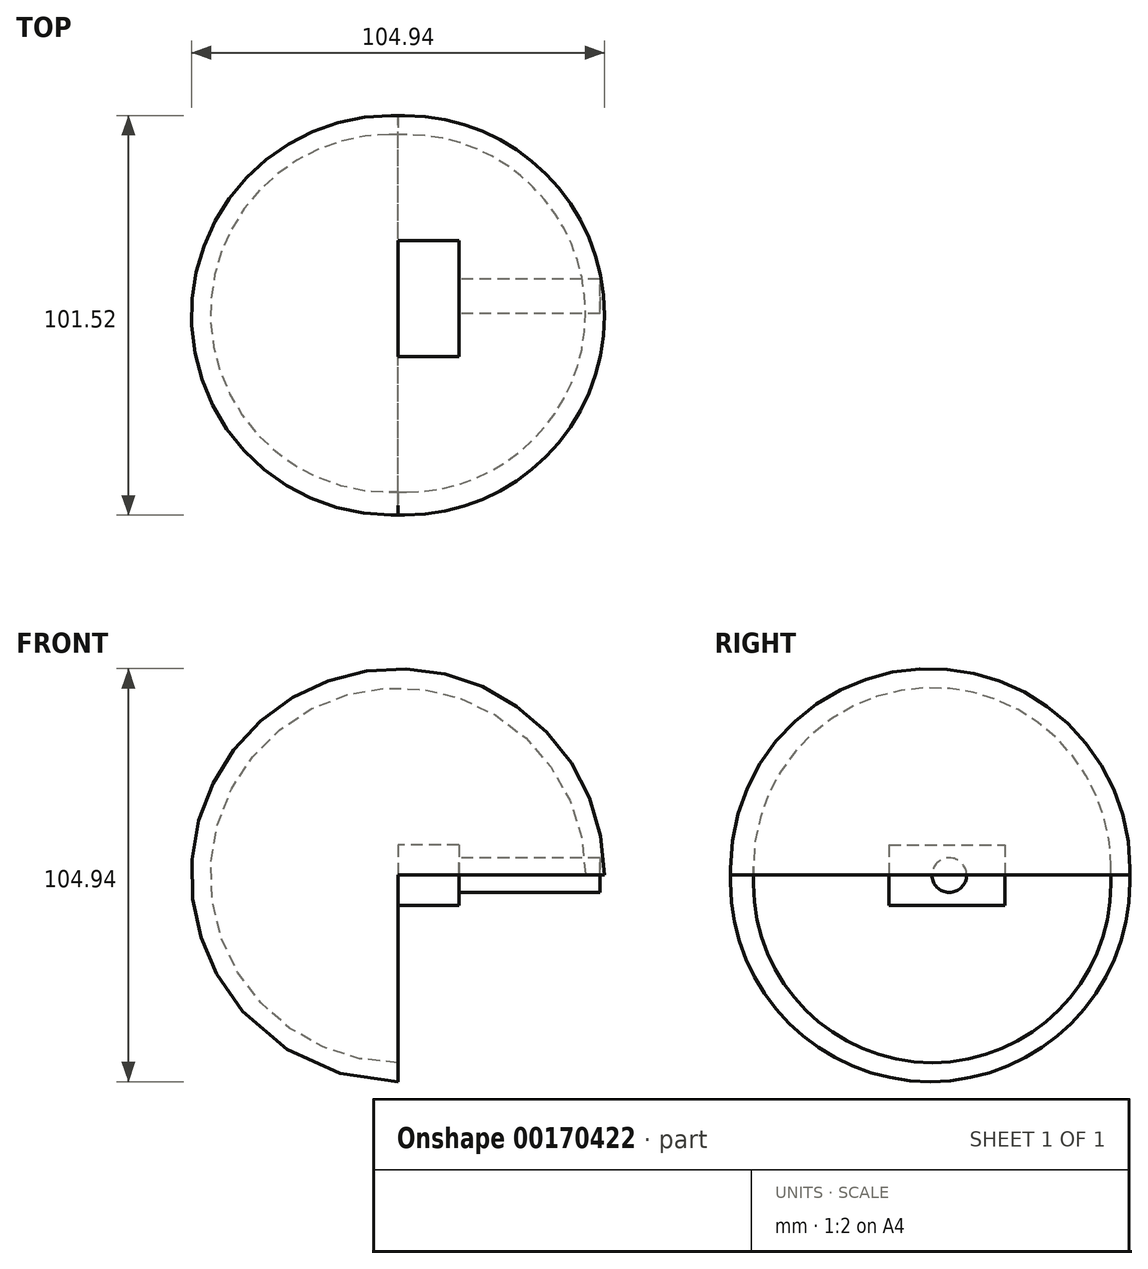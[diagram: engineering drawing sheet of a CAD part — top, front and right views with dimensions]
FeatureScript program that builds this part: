
annotation { "Feature Type Name" : "Feature", "Feature Type Description" : "" }
export const myFeature = defineFeature(function(context is Context, id is Id, definition is map)
    precondition{}
    {
        {
            var Q0;
            Q0=qCreatedBy(makeId("Top.planeOp"),FACE);
            var sketch = newSketch(context, id + "F0", { "sketchPlane" : qUnion([Q0])});
            skLineSegment(sketch, "E0", {"start": v(0, 45.88) * mm, "end": v(0, -55.58) * mm});
            skArc(sketch, "E1", {"start": v(0, -55.58) * mm, "mid": v(52.47, -4.85) * mm, "end": v(0, 45.88) * mm});
            skLineSegment(sketch, "E2", {"start": v(0, 60.6) * mm, "end": v(0, -69.99) * mm});
            skArc(sketch, "E3", {"start": v(0, -49.72) * mm, "mid": v(47.63, -4.35) * mm, "end": v(0, 41.02) * mm});
            skSolve(sketch);
        }
        {
            var Q0;
            {var subQ0=sQuery(id+"F0.wireOp",EDGE,"E1");Q0=makeQuery(id+"F0.imprint","IMPRINT",FACE,{"disambiguationData":[TD([[makeQuery(id+"F0.imprint","IMPRINT",EDGE,{"derivedFrom":subQ0}),1.0]])]});}
            var Q1;
            Q1=sQuery(id+"F0.wireOp",EDGE,"E2");
            revolve(context, id + "F1", {"entities" : qUnion([Q0]), "axis" : qUnion([Q1]), "revolveType" : RevolveType.ONE_DIRECTION, "angle" : 270 * degree});
        }
        {
            var Q0;
            Q0=qCreatedBy(makeId("Right.planeOp"),FACE);
            var sketch = newSketch(context, id + "F2", { "sketchPlane" : qUnion([Q0])});
            skLineSegment(sketch, "E4.bottom", {"start": v(-15.34, 7.67) * mm, "end": v(14.1, 7.67) * mm});
            skLineSegment(sketch, "E4.top", {"start": v(-15.34, -7.67) * mm, "end": v(14.1, -7.67) * mm});
            skLineSegment(sketch, "E4.left", {"start": v(-15.34, 7.67) * mm, "end": v(-15.34, -7.67) * mm});
            skLineSegment(sketch, "E4.right", {"start": v(14.1, 7.67) * mm, "end": v(14.1, -7.67) * mm});
            skSolve(sketch);
        }
        {
            var Q0;
            Q0 = qSketchRegion(id + "F2", true);
            extrude(context, id + "F3", {"entities" : qUnion([Q0]), "depth" : 15.5 * mm});
        }
        {
            var Q0;
            Q0=makeQuery(id+"F3.opExtrude","CAP_FACE",FACE,{"disambiguationData":[OSD([sQuery(id+"F2.wireOp",EDGE,"E4.bottom"),sQuery(id+"F2.wireOp",EDGE,"E4.top"),sQuery(id+"F2.wireOp",EDGE,"E4.left"),sQuery(id+"F2.wireOp",EDGE,"E4.right")])],"isStart":false});
            var sketch = newSketch(context, id + "F4", { "sketchPlane" : qUnion([Q0])});
            skCircle(sketch, "E5", {"center": v(0, 0) * mm, "radius": 4.4 * mm});
            skSolve(sketch);
        }
        {
            var Q0;
            Q0 = qSketchRegion(id + "F4", true);
            extrude(context, id + "F5", {"entities" : qUnion([Q0]), "depth" : 35.81 * mm});
        }
    });
